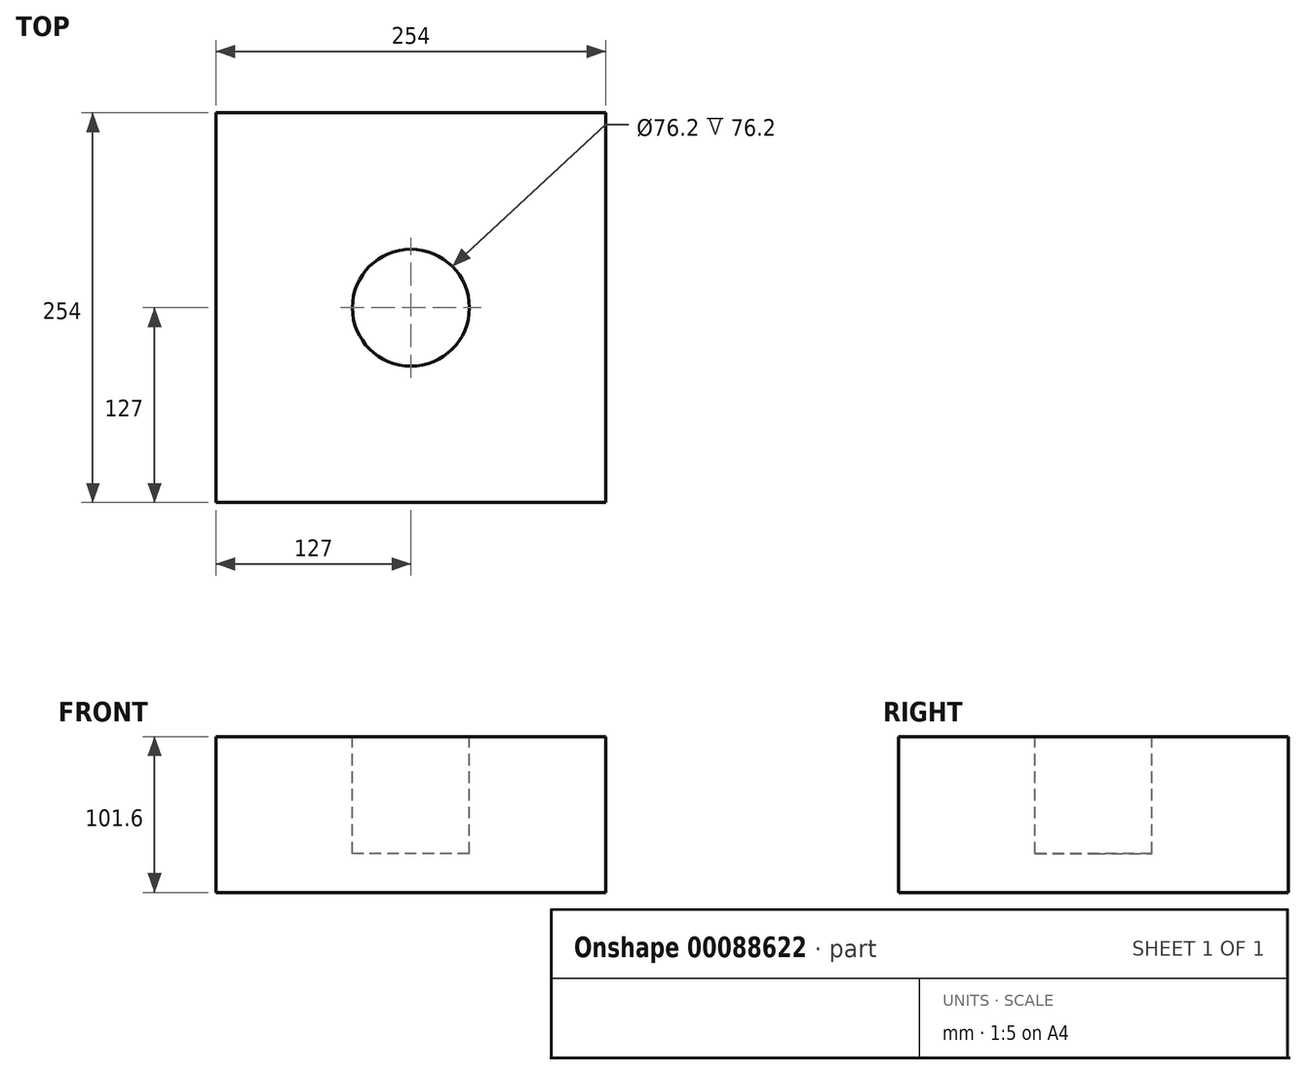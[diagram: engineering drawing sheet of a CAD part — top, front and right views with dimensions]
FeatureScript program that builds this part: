
annotation { "Feature Type Name" : "Feature", "Feature Type Description" : "" }
export const myFeature = defineFeature(function(context is Context, id is Id, definition is map)
    precondition{}
    {
        {
            var Q0;
            Q0=qCreatedBy(makeId("Top.planeOp"),FACE);
            var sketch = newSketch(context, id + "F0", { "sketchPlane" : qUnion([Q0])});
            skLineSegment(sketch, "E0.bottom", {"start": v(127, -127) * mm, "end": v(-127, -127) * mm});
            skLineSegment(sketch, "E0.top", {"start": v(127, 127) * mm, "end": v(-127, 127) * mm});
            skLineSegment(sketch, "E0.left", {"start": v(127, -127) * mm, "end": v(127, 127) * mm});
            skLineSegment(sketch, "E0.right", {"start": v(-127, -127) * mm, "end": v(-127, 127) * mm});
            skPoint(sketch, "E0.middle", {"position": v(0, 0) * mm});
            skSolve(sketch);
        }
        {
            var Q0;
            Q0 = qSketchRegion(id + "F0", true);
            extrude(context, id + "F1", {"entities" : qUnion([Q0]), "depth" : 101.6 * mm});
        }
        {
            var Q0;
            Q0=makeQuery(id+"F1.opExtrude","CAP_FACE",FACE,{"disambiguationData":[OSD([sQuery(id+"F0.wireOp",EDGE,"E0.bottom"),sQuery(id+"F0.wireOp",EDGE,"E0.top"),sQuery(id+"F0.wireOp",EDGE,"E0.left"),sQuery(id+"F0.wireOp",EDGE,"E0.right")])],"isStart":false});
            var sketch = newSketch(context, id + "F2", { "sketchPlane" : qUnion([Q0])});
            skCircle(sketch, "E1", {"center": v(0, 0) * mm, "radius": 38.1 * mm});
            skSolve(sketch);
        }
        {
            var Q0;
            Q0 = qSketchRegion(id + "F2", true);
            extrude(context, id + "F3", {"entities" : qUnion([Q0]), "operationType" : NewBodyOperationType.REMOVE, "oppositeDirection" : true, "depth" : 76.2 * mm});
        }
    });
